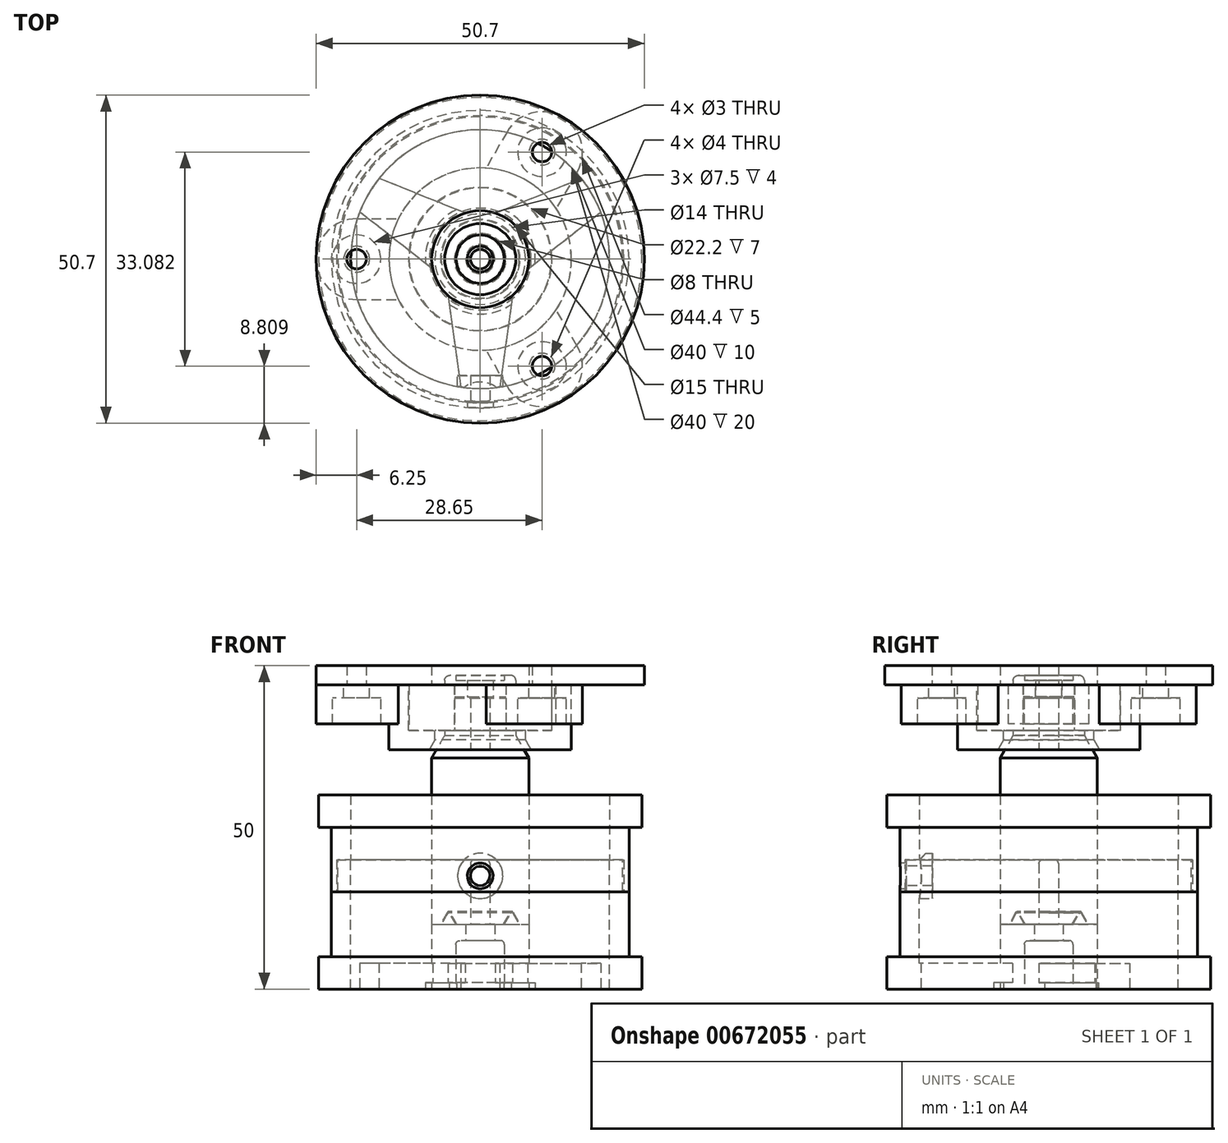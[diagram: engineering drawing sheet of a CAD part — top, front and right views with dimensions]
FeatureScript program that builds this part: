
annotation { "Feature Type Name" : "Feature", "Feature Type Description" : "" }
export const myFeature = defineFeature(function(context is Context, id is Id, definition is map)
    precondition{}
    {
        {
            var Q0;
            Q0=qCreatedBy(makeId("Top.planeOp"),FACE);
            var sketch = newSketch(context, id + "F0", { "sketchPlane" : qUnion([Q0])});
            skCircle(sketch, "E0", {"center": v(0, 0) * mm, "radius": 11.07 * mm});
            skCircle(sketch, "E1", {"center": v(0, 0) * mm, "radius": 13.75 * mm});
            skCircle(sketch, "E2", {"center": v(0, 0) * mm, "radius": 20 * mm});
            skCircle(sketch, "E3", {"center": v(0, 0) * mm, "radius": 25 * mm});
            skCircle(sketch, "E4", {"center": v(0, 0) * mm, "radius": 7.5 * mm});
            skSolve(sketch);
        }
        {
            var Q0;
            Q0=qCreatedBy(makeId("Front.planeOp"),FACE);
            var sketch = newSketch(context, id + "F1", { "sketchPlane" : qUnion([Q0])});
            skPoint(sketch, "E5.0", {"position": v(0, 0) * mm});
            skLineSegment(sketch, "E6", {"start": v(20, 30) * mm, "end": v(20, 0) * mm, "construction": true});
            skLineSegment(sketch, "E7", {"start": v(25, 30) * mm, "end": v(25, 0) * mm, "construction": true});
            skLineSegment(sketch, "E8", {"start": v(25, 30) * mm, "end": v(25, 25) * mm});
            skLineSegment(sketch, "E9", {"start": v(25, 25) * mm, "end": v(23, 25) * mm});
            skLineSegment(sketch, "E10", {"start": v(23, 25) * mm, "end": v(23, 15) * mm});
            skLineSegment(sketch, "E11", {"start": v(25, 30) * mm, "end": v(20, 30) * mm});
            skLineSegment(sketch, "E12", {"start": v(20, 15) * mm, "end": v(20, 30) * mm});
            skLineSegment(sketch, "E13", {"start": v(20, 15) * mm, "end": v(23, 15) * mm});
            skLineSegment(sketch, "E14.MirrorCS", {"start": v(23, 5) * mm, "end": v(23, 15) * mm});
            skLineSegment(sketch, "E15.MirrorCS", {"start": v(25, 0) * mm, "end": v(25, 5) * mm});
            skLineSegment(sketch, "E16.MirrorCS", {"start": v(25, 5) * mm, "end": v(23, 5) * mm});
            skLineSegment(sketch, "E17.MirrorCS", {"start": v(25, 0) * mm, "end": v(20, 0) * mm});
            skLineSegment(sketch, "E18.MirrorCS", {"start": v(20, 15) * mm, "end": v(20, 0) * mm});
            skLineSegment(sketch, "E19", {"start": v(25, 25) * mm, "end": v(25, 5) * mm});
            skSolve(sketch);
        }
        {
            var Q0;
            Q0=qCreatedBy(makeId("Front.planeOp"),FACE);
            var sketch = newSketch(context, id + "F2", { "sketchPlane" : qUnion([Q0])});
            skLineSegment(sketch, "E20.0.0", {"start": v(23, 15) * mm, "end": v(20, 15) * mm});
            skLineSegment(sketch, "E20.0.1", {"start": v(20, 15) * mm, "end": v(20, 0) * mm});
            skLineSegment(sketch, "E20.0.2", {"start": v(20, 0) * mm, "end": v(25, 0) * mm});
            skLineSegment(sketch, "E20.0.3", {"start": v(25, 0) * mm, "end": v(25, 5) * mm});
            skLineSegment(sketch, "E20.0.4", {"start": v(25, 5) * mm, "end": v(23, 5) * mm});
            skLineSegment(sketch, "E20.0.5", {"start": v(23, 5) * mm, "end": v(23, 15) * mm});
            skLineSegment(sketch, "E21", {"start": v(20, 15) * mm, "end": v(20, 20) * mm});
            skLineSegment(sketch, "E22", {"start": v(20, 20) * mm, "end": v(22, 20) * mm});
            skLineSegment(sketch, "E23", {"start": v(22, 20) * mm, "end": v(22, 15) * mm});
            skSolve(sketch);
        }
        {
            var Q0;
            Q0=qCreatedBy(makeId("Front.planeOp"),FACE);
            var sketch = newSketch(context, id + "F3", { "sketchPlane" : qUnion([Q0])});
            skLineSegment(sketch, "E24.0.0", {"start": v(20, 30) * mm, "end": v(20, 15) * mm});
            skLineSegment(sketch, "E24.0.1", {"start": v(20, 15) * mm, "end": v(23, 15) * mm});
            skLineSegment(sketch, "E24.0.2", {"start": v(23, 15) * mm, "end": v(23, 25) * mm});
            skLineSegment(sketch, "E24.0.3", {"start": v(23, 25) * mm, "end": v(25, 25) * mm});
            skLineSegment(sketch, "E24.0.4", {"start": v(25, 25) * mm, "end": v(25, 30) * mm});
            skLineSegment(sketch, "E24.0.5", {"start": v(25, 30) * mm, "end": v(20, 30) * mm});
            skLineSegment(sketch, "E25.0", {"start": v(22.2, 20) * mm, "end": v(22.2, 15) * mm});
            skLineSegment(sketch, "E26.0", {"start": v(20, 20) * mm, "end": v(22, 20) * mm, "construction": true});
            skLineSegment(sketch, "E27", {"start": v(20, 20) * mm, "end": v(22.2, 20) * mm});
            skSolve(sketch);
        }
        {
            var Q0;
            Q0=qCreatedBy(makeId("Top.planeOp"),FACE);
            var sketch = newSketch(context, id + "F4", { "sketchPlane" : qUnion([Q0])});
            skCircle(sketch, "E28", {"center": v(0, 0) * mm, "radius": 2.25 * mm});
            skCircle(sketch, "E29", {"center": v(0, 0) * mm, "radius": 3.75 * mm});
            skCircle(sketch, "E30", {"center": v(0, 0) * mm, "radius": 7.5 * mm});
            skSolve(sketch);
        }
        {
            var Q0;
            Q0=makeQuery(id+"F4.imprint","IMPRINT",FACE,{"disambiguationData":[TD([[makeQuery(id+"F4.imprint","IMPRINT",EDGE,{"derivedFrom":sQuery(id+"F4.wireOp",EDGE,"E29")}),-1.0]])]});
            var Q1;
            Q1=makeQuery(id+"F4.imprint","IMPRINT",FACE,{"disambiguationData":[TD([[makeQuery(id+"F4.imprint","IMPRINT",EDGE,{"derivedFrom":sQuery(id+"F4.wireOp",EDGE,"E28")}),-1.0]])]});
            extrude(context, id + "F5", {"entities" : qUnion([Q0, Q1]), "depth" : 10 * mm, "offsetDistance" : 25 * mm});
        }
        {
            var Q0;
            Q0=makeQuery(id+"F4.imprint","IMPRINT",FACE,{"disambiguationData":[TD([[makeQuery(id+"F4.imprint","IMPRINT",EDGE,{"derivedFrom":sQuery(id+"F4.wireOp",EDGE,"E28")}),-1.0]])]});
            extrude(context, id + "F6", {"entities" : qUnion([Q0]), "operationType" : NewBodyOperationType.REMOVE, "depth" : 7.5 * mm, "offsetDistance" : 25 * mm});
        }
        {
            var Q0;
            Q0=qCreatedBy(makeId("Front.planeOp"),FACE);
            var sketch = newSketch(context, id + "F7", { "sketchPlane" : qUnion([Q0])});
            skLineSegment(sketch, "E31.0.0", {"start": v(-7.5, 10) * mm, "end": v(7.5, 10) * mm});
            skLineSegment(sketch, "E32.0", {"start": v(-20, 0) * mm, "end": v(20, 0) * mm});
            skLineSegment(sketch, "E33", {"start": v(-7.5, 0) * mm, "end": v(-7.5, 10) * mm});
            skLineSegment(sketch, "E34", {"start": v(7.5, 10) * mm, "end": v(7.5, 0) * mm});
            skLineSegment(sketch, "E35", {"start": v(-2.25, 7.5) * mm, "end": v(-2.25, 10) * mm});
            skLineSegment(sketch, "E36", {"start": v(2.25, 10) * mm, "end": v(2.25, 7.5) * mm});
            skLineSegment(sketch, "E37", {"start": v(-2.25, 10) * mm, "end": v(-7.5, 10) * mm});
            skLineSegment(sketch, "E38", {"start": v(-4.88, 10) * mm, "end": v(-4.88, 12) * mm, "construction": true});
            skLineSegment(sketch, "E39", {"start": v(-4.88, 12) * mm, "end": v(-6.03, 10) * mm});
            skLineSegment(sketch, "E40.MirrorCS", {"start": v(-4.88, 12) * mm, "end": v(-3.72, 10) * mm});
            skSolve(sketch);
        }
        {
            var Q0;
            {var subQ0=sQuery(id+"F7.wireOp",EDGE,"E39");Q0=makeQuery(id+"F7.imprint","IMPRINT",FACE,{"disambiguationData":[TD([[makeQuery(id+"F7.imprint","IMPRINT",EDGE,{"derivedFrom":subQ0}),1.0]])]});}
            var Q1;
            Q1=makeQuery(id+"F5.opExtrude","SWEPT_FACE",FACE,{"disambiguationData":[OSD([sQuery(id+"F4.wireOp",EDGE,"E28")])]});
            revolve(context, id + "F8", {"operationType" : NewBodyOperationType.ADD, "entities" : qUnion([Q0]), "axis" : qUnion([Q1]), "revolveType" : RevolveType.FULL});
        }
        {
            var Q0;
            Q0=qCreatedBy(makeId("Front.planeOp"),FACE);
            var sketch = newSketch(context, id + "F9", { "sketchPlane" : qUnion([Q0])});
            skLineSegment(sketch, "E41.0", {"start": v(-7.5, 10) * mm, "end": v(7.5, 10) * mm});
            skLineSegment(sketch, "E42", {"start": v(0, 0) * mm, "end": v(0, 10) * mm, "construction": true});
            skLineSegment(sketch, "E43", {"start": v(0, 10) * mm, "end": v(0, 45) * mm});
            skLineSegment(sketch, "E44", {"start": v(7.5, 10) * mm, "end": v(7.5, 45) * mm});
            skLineSegment(sketch, "E45", {"start": v(7.5, 45) * mm, "end": v(0, 45) * mm});
            skLineSegment(sketch, "E46", {"start": v(7.5, 45) * mm, "end": v(7.5, 40) * mm, "construction": true});
            skLineSegment(sketch, "E47", {"start": v(7.5, 40) * mm, "end": v(0, 40) * mm, "construction": true});
            skLineSegment(sketch, "E48", {"start": v(0, 40) * mm, "end": v(3.95, 40) * mm, "construction": true});
            skLineSegment(sketch, "E49", {"start": v(3.95, 40) * mm, "end": v(3.95, 45) * mm});
            skLineSegment(sketch, "E50", {"start": v(3.95, 40) * mm, "end": v(7.5, 40) * mm});
            skLineSegment(sketch, "E51", {"start": v(0, 10) * mm, "end": v(0, 20) * mm, "construction": true});
            skLineSegment(sketch, "E52", {"start": v(0, 20) * mm, "end": v(1.5, 20) * mm});
            skLineSegment(sketch, "E53", {"start": v(1.5, 20) * mm, "end": v(1.5, 10) * mm});
            skLineSegment(sketch, "E54", {"start": v(1.5, 10) * mm, "end": v(0, 10) * mm});
            skLineSegment(sketch, "E55", {"start": v(0, 45) * mm, "end": v(1.5, 45) * mm});
            skLineSegment(sketch, "E56", {"start": v(1.5, 45) * mm, "end": v(1.5, 40) * mm});
            skLineSegment(sketch, "E57", {"start": v(1.5, 40) * mm, "end": v(0, 40) * mm});
            skLineSegment(sketch, "E58", {"start": v(4.88, 12) * mm, "end": v(3.72, 10) * mm});
            skLineSegment(sketch, "E59", {"start": v(-6.03, 10) * mm, "end": v(-4.88, 12) * mm});
            skLineSegment(sketch, "E60", {"start": v(4.88, 12) * mm, "end": v(6.03, 10) * mm});
            skLineSegment(sketch, "E61.0.0", {"start": v(-3.72, 10) * mm, "end": v(3.72, 10) * mm});
            skLineSegment(sketch, "E62.0", {"start": v(4.88, 12.2) * mm, "end": v(3.6, 10) * mm});
            skLineSegment(sketch, "E62.1", {"start": v(4.88, 12.2) * mm, "end": v(6.15, 10) * mm});
            skLineSegment(sketch, "E63", {"start": v(7.5, 45) * mm, "end": v(7.5, 45.2) * mm, "construction": true});
            skLineSegment(sketch, "E64", {"start": v(7.5, 45.2) * mm, "end": v(0, 45.2) * mm, "construction": true});
            skLineSegment(sketch, "E65", {"start": v(0, 40) * mm, "end": v(5.5, 40) * mm});
            skLineSegment(sketch, "E66", {"start": v(5.5, 40) * mm, "end": v(5.5, 39.2) * mm});
            skLineSegment(sketch, "E67", {"start": v(5.5, 39.2) * mm, "end": v(7.5, 39.2) * mm});
            skLineSegment(sketch, "E68", {"start": v(3.95, 45) * mm, "end": v(3.95, 45.2) * mm, "construction": true});
            skLineSegment(sketch, "E69", {"start": v(3.95, 45.2) * mm, "end": v(3.95, 47) * mm});
            skLineSegment(sketch, "E70", {"start": v(5.5, 40) * mm, "end": v(5.5, 47) * mm, "construction": true});
            skLineSegment(sketch, "E71", {"start": v(5.5, 47) * mm, "end": v(3.95, 47) * mm});
            skLineSegment(sketch, "E72", {"start": v(5.5, 47) * mm, "end": v(5.5, 48.5) * mm});
            skLineSegment(sketch, "E73", {"start": v(5.5, 48.5) * mm, "end": v(0, 48.5) * mm});
            skLineSegment(sketch, "E74", {"start": v(0, 48.5) * mm, "end": v(0, 45.2) * mm});
            skLineSegment(sketch, "E75", {"start": v(3.95, 45.2) * mm, "end": v(0, 45.2) * mm});
            skLineSegment(sketch, "E76", {"start": v(0, 48.5) * mm, "end": v(1.88, 48.5) * mm});
            skLineSegment(sketch, "E77", {"start": v(0, 45.2) * mm, "end": v(2, 45.2) * mm, "construction": true});
            skLineSegment(sketch, "E78", {"start": v(2, 45.2) * mm, "end": v(2, 47.7) * mm});
            skLineSegment(sketch, "E79", {"start": v(0, 48.5) * mm, "end": v(3.75, 48.5) * mm, "construction": true});
            skLineSegment(sketch, "E80", {"start": v(3.75, 48.5) * mm, "end": v(3.75, 47.7) * mm});
            skLineSegment(sketch, "E81", {"start": v(3.75, 47.7) * mm, "end": v(2, 47.7) * mm});
            skLineSegment(sketch, "E82", {"start": v(5.5, 39.2) * mm, "end": v(7.5, 35.74) * mm});
            skLineSegment(sketch, "E83", {"start": v(1.5, 40) * mm, "end": v(1.5, 37) * mm});
            skLineSegment(sketch, "E84", {"start": v(1.5, 37) * mm, "end": v(0, 37) * mm});
            skSolve(sketch);
        }
        {
            var Q0;
            {var subQ4=sQuery(id+"F9.wireOp",EDGE,"E52");Q0=makeQuery(id+"F9.imprint","IMPRINT",FACE,{"disambiguationData":[TD([[makeQuery(id+"F9.imprint","IMPRINT",EDGE,{"derivedFrom":subQ4}),1.0]])]});}
            var Q1;
            {var subQ2=sQuery(id+"F9.wireOp",EDGE,"E49");Q1=makeQuery(id+"F9.imprint","IMPRINT",FACE,{"disambiguationData":[TD([[makeQuery(id+"F9.imprint","IMPRINT",EDGE,{"derivedFrom":subQ2}),1.0]])]});}
            var Q2;
            {var subQ3=sQuery(id+"F9.wireOp",EDGE,"E69");Q2=makeQuery(id+"F9.imprint","IMPRINT",FACE,{"disambiguationData":[TD([[makeQuery(id+"F9.imprint","IMPRINT",EDGE,{"derivedFrom":subQ3}),1.0]])]});}
            var Q3;
            Q3=sQuery(id+"F9.wireOp",EDGE,"E43");
            revolve(context, id + "F10", {"entities" : qUnion([Q0, Q1, Q2]), "axis" : qUnion([Q3]), "revolveType" : RevolveType.FULL});
        }
        {
            var Q0;
            Q0=makeQuery(id+"F8.opRevolve","SWEPT_EDGE",EDGE,{"disambiguationData":[OSD([sQuery(id+"F7.wireOp",EDGE,"E39"),sQuery(id+"F7.wireOp",EDGE,"E40.MirrorCS")])]});
            var Q1;
            Q1=makeQuery(id+"F10.opRevolve","SWEPT_EDGE",EDGE,{"disambiguationData":[OSD([sQuery(id+"F9.wireOp",EDGE,"E62.0"),sQuery(id+"F9.wireOp",EDGE,"E62.1")])]});
            fillet(context, id + "F11", {"entities" : qUnion([Q0, Q1]), "radius" : .2 * mm, "tangentPropagation" : true, "allowEdgeOverflow" : false});
        }
        {
            var Q0;
            Q0=makeQuery(id+"F10.opRevolve","SWEPT_EDGE",EDGE,{"disambiguationData":[OSD([sQuery(id+"F9.wireOp",EDGE,"E52"),sQuery(id+"F9.wireOp",EDGE,"E53")])]});
            var Q1;
            Q1=makeQuery(id+"F6.boolean.opBoolean","COPY",EDGE,{"derivedFrom":makeQuery(id+"F6.opExtrude","CAP_EDGE",EDGE,{"disambiguationData":[OSD([sQuery(id+"F4.wireOp",EDGE,"E28")])],"isStart":false})});
            var Q2;
            Q2=makeQuery(id+"F6.boolean.opBoolean","COPY",EDGE,{"derivedFrom":makeQuery(id+"F6.opExtrude","CAP_EDGE",EDGE,{"disambiguationData":[OSD([sQuery(id+"F4.wireOp",EDGE,"E29")])],"isStart":false})});
            fillet(context, id + "F12", {"entities" : qUnion([Q0, Q1, Q2]), "radius" : .6 * mm, "tangentPropagation" : true, "allowEdgeOverflow" : false});
        }
        {
            var Q0;
            Q0=makeQuery(id+"F10.opRevolve","SWEPT_EDGE",EDGE,{"disambiguationData":[OSD([sQuery(id+"F9.wireOp",EDGE,"E72"),sQuery(id+"F9.wireOp",EDGE,"E73")])]});
            fillet(context, id + "F13", {"entities" : qUnion([Q0]), "radius" : .8 * mm, "tangentPropagation" : true, "allowEdgeOverflow" : false});
        }
        {
            var Q0;
            Q0=qCreatedBy(makeId("Front.planeOp"),FACE);
            var sketch = newSketch(context, id + "F14", { "sketchPlane" : qUnion([Q0])});
            skLineSegment(sketch, "E85.0.0", {"start": v(-5.5, 40) * mm, "end": v(5.5, 40) * mm, "construction": true});
            skLineSegment(sketch, "E86", {"start": v(-3.95, 40) * mm, "end": v(-3.95, 45) * mm, "construction": true});
            skLineSegment(sketch, "E87", {"start": v(3.95, 45) * mm, "end": v(3.95, 40) * mm, "construction": true});
            skLineSegment(sketch, "E88.0.0", {"start": v(5.5, 47) * mm, "end": v(-5.5, 47) * mm, "construction": true});
            skLineSegment(sketch, "E89", {"start": v(-3.95, 45.2) * mm, "end": v(-3.95, 47) * mm, "construction": true});
            skLineSegment(sketch, "E90", {"start": v(3.95, 47) * mm, "end": v(3.95, 45.2) * mm, "construction": true});
            skLineSegment(sketch, "E91", {"start": v(-5.5, 47) * mm, "end": v(-5.5, 40) * mm});
            skLineSegment(sketch, "E92", {"start": v(0, 40) * mm, "end": v(0, 47) * mm, "construction": true});
            skLineSegment(sketch, "E93", {"start": v(0, 43.5) * mm, "end": v(-11, 43.5) * mm, "construction": true});
            skLineSegment(sketch, "E94", {"start": v(-11, 43.5) * mm, "end": v(-11, 47) * mm});
            skLineSegment(sketch, "E95", {"start": v(-11, 47) * mm, "end": v(-5.5, 47) * mm});
            skLineSegment(sketch, "E96", {"start": v(-11, 43.5) * mm, "end": v(-11, 40) * mm});
            skLineSegment(sketch, "E97", {"start": v(-11, 40) * mm, "end": v(-5.5, 40) * mm});
            skLineSegment(sketch, "E98", {"start": v(-3.95, 40) * mm, "end": v(-3.95, 47) * mm});
            skLineSegment(sketch, "E99", {"start": v(0, 43.5) * mm, "end": v(-4, 43.5) * mm, "construction": true});
            skLineSegment(sketch, "E100", {"start": v(-4, 43.5) * mm, "end": v(-4, 47) * mm});
            skLineSegment(sketch, "E101", {"start": v(-4, 47) * mm, "end": v(-5.5, 47) * mm});
            skLineSegment(sketch, "E102", {"start": v(-4, 43.5) * mm, "end": v(-4, 40) * mm});
            skLineSegment(sketch, "E103", {"start": v(-4, 40) * mm, "end": v(-5.5, 40) * mm});
            skSolve(sketch);
        }
        {
            var Q0;
            Q0=makeQuery(id+"F14.imprint","IMPRINT",FACE,{"disambiguationData":[TD([[makeQuery(id+"F14.imprint","IMPRINT",EDGE,{"derivedFrom":sQuery(id+"F14.wireOp",EDGE,"E91")}),-1.0]])]});
            var Q1;
            Q1=makeQuery(id+"F14.imprint","IMPRINT",FACE,{"disambiguationData":[TD([[makeQuery(id+"F14.imprint","IMPRINT",EDGE,{"derivedFrom":sQuery(id+"F14.wireOp",EDGE,"E91")}),1.0]])]});
            var Q2;
            Q2=sQuery(id+"F14.wireOp",EDGE,"E92");
            revolve(context, id + "F15", {"entities" : qUnion([Q0, Q1]), "axis" : qUnion([Q2]), "revolveType" : RevolveType.FULL});
        }
        {
            var Q0;
            Q0=qCreatedBy(makeId("Front.planeOp"),FACE);
            var sketch = newSketch(context, id + "F16", { "sketchPlane" : qUnion([Q0])});
            skLineSegment(sketch, "E104", {"start": v(-1.5, 40) * mm, "end": v(-1.5, 45) * mm, "construction": true});
            skLineSegment(sketch, "E105", {"start": v(1.5, 45) * mm, "end": v(1.5, 40) * mm, "construction": true});
            skLineSegment(sketch, "E106.0.0", {"start": v(3.95, 40) * mm, "end": v(-3.95, 40) * mm, "construction": true});
            skLineSegment(sketch, "E107.0.0", {"start": v(-3.95, 45) * mm, "end": v(3.95, 45) * mm, "construction": true});
            skLineSegment(sketch, "E108", {"start": v(0, 45) * mm, "end": v(0, 40) * mm, "construction": true});
            skLineSegment(sketch, "E109.0.0", {"start": v(11, 40) * mm, "end": v(-11, 40) * mm, "construction": true});
            skLineSegment(sketch, "E110", {"start": v(-11, 40) * mm, "end": v(-11, 47) * mm, "construction": true});
            skLineSegment(sketch, "E111", {"start": v(11, 47) * mm, "end": v(11, 40) * mm, "construction": true});
            skLineSegment(sketch, "E112", {"start": v(-7.5, 35.74) * mm, "end": v(-5.5, 39.2) * mm, "construction": true});
            skLineSegment(sketch, "E113", {"start": v(5.5, 39.2) * mm, "end": v(7.5, 35.74) * mm, "construction": true});
            skLineSegment(sketch, "E114", {"start": v(-5.5, 39.2) * mm, "end": v(-5.5, 40) * mm, "construction": true});
            skLineSegment(sketch, "E115", {"start": v(5.5, 40) * mm, "end": v(5.5, 39.2) * mm, "construction": true});
            skLineSegment(sketch, "E116", {"start": v(-5.5, 40) * mm, "end": v(-7, 40) * mm, "construction": true});
            skLineSegment(sketch, "E117", {"start": v(-7, 40) * mm, "end": v(-7, 38.5) * mm});
            skLineSegment(sketch, "E118", {"start": v(0, 40) * mm, "end": v(-11.1, 40) * mm});
            skLineSegment(sketch, "E119", {"start": v(-11.1, 40) * mm, "end": v(-11.1, 47.44) * mm});
            skLineSegment(sketch, "E120", {"start": v(-11.1, 47) * mm, "end": v(-14.1, 47) * mm});
            skLineSegment(sketch, "E121", {"start": v(-7, 38.5) * mm, "end": v(-7.87, 37) * mm});
            skLineSegment(sketch, "E122", {"start": v(-7.87, 37) * mm, "end": v(-14.1, 37) * mm});
            skLineSegment(sketch, "E123", {"start": v(-14.1, 37) * mm, "end": v(-14.1, 47) * mm});
            skLineSegment(sketch, "E124", {"start": v(-14.1, 47) * mm, "end": v(-24.1, 47) * mm});
            skLineSegment(sketch, "E125", {"start": v(-24.1, 47) * mm, "end": v(-24.1, 44) * mm});
            skLineSegment(sketch, "E126", {"start": v(-24.1, 44) * mm, "end": v(-14.1, 44) * mm});
            skSolve(sketch);
        }
        {
            var Q0;
            {var subQ4=sQuery(id+"F16.wireOp",EDGE,"E117");Q0=makeQuery(id+"F16.imprint","IMPRINT",FACE,{"disambiguationData":[TD([[makeQuery(id+"F16.imprint","IMPRINT",EDGE,{"derivedFrom":subQ4}),-1.0]])]});}
            var Q1;
            Q1=sQuery(id+"F16.wireOp",EDGE,"E108");
            revolve(context, id + "F17", {"entities" : qUnion([Q0]), "axis" : qUnion([Q1]), "revolveType" : RevolveType.FULL});
        }
        {
            var Q0;
            Q0=makeQuery(id+"F17.opRevolve","SWEPT_FACE",FACE,{"disambiguationData":[OSD([sQuery(id+"F16.wireOp",EDGE,"E120")])]});
            var sketch = newSketch(context, id + "F18", { "sketchPlane" : qUnion([Q0])});
            skCircle(sketch, "E127.0", {"center": v(0, 0) * mm, "radius": 14.1 * mm, "construction": true});
            skLineSegment(sketch, "E128.0", {"start": v(-24.1, 0) * mm, "end": v(-14.1, 0) * mm, "construction": true});
            skCircle(sketch, "E129", {"center": v(-19.1, 0) * mm, "radius": 3.75 * mm});
            skCircle(sketch, "E130", {"center": v(-19.1, 0) * mm, "radius": 2 * mm});
            skCircle(sketch, "E131", {"center": v(-19.1, 0) * mm, "radius": 6.25 * mm});
            skLineSegment(sketch, "E132", {"start": v(-19.1, 0) * mm, "end": v(-19.1, 6.25) * mm, "construction": true});
            skLineSegment(sketch, "E133", {"start": v(-19.1, 0) * mm, "end": v(-19.1, -6.25) * mm, "construction": true});
            skLineSegment(sketch, "E134", {"start": v(-19.1, -6.25) * mm, "end": v(-12.64, -6.25) * mm});
            skLineSegment(sketch, "E135", {"start": v(-19.1, 6.25) * mm, "end": v(-12.64, 6.25) * mm});
            skLineSegment(sketch, "E136", {"start": v(0, 0) * mm, "end": v(0, 7.47) * mm});
            skCircle(sketch, "E137.MirrorC", {"center": v(19.1, 0) * mm, "radius": 6.25 * mm});
            skCircle(sketch, "E138.MirrorC", {"center": v(19.1, 0) * mm, "radius": 2 * mm});
            skCircle(sketch, "E139.MirrorC", {"center": v(19.1, 0) * mm, "radius": 3.75 * mm});
            skLineSegment(sketch, "E140.MirrorCS", {"start": v(19.1, 6.25) * mm, "end": v(12.64, 6.25) * mm});
            skLineSegment(sketch, "E141.MirrorCS", {"start": v(19.1, -6.25) * mm, "end": v(12.64, -6.25) * mm});
            skSolve(sketch);
        }
        {
            var Q0;
            Q0=makeQuery(id+"F18.imprint","IMPRINT",FACE,{"disambiguationData":[TD([[makeQuery(id+"F18.imprint","IMPRINT",EDGE,{"derivedFrom":sQuery(id+"F18.wireOp",EDGE,"E129")}),1.0]])]});
            var Q1;
            Q1=makeQuery(id+"F18.imprint","IMPRINT",FACE,{"disambiguationData":[TD([[makeQuery(id+"F18.imprint","IMPRINT",EDGE,{"derivedFrom":sQuery(id+"F18.wireOp",EDGE,"E129")}),-1.0]])]});
            var Q2;
            {var subQ0=sQuery(id+"F18.wireOp",EDGE,"E134");Q2=makeQuery(id+"F18.imprint","IMPRINT",FACE,{"disambiguationData":[TD([[makeQuery(id+"F18.imprint","IMPRINT",EDGE,{"derivedFrom":subQ0}),1.0]])]});}
            var Q3;
            {var subQ0=sQuery(id+"F18.wireOp",EDGE,"E135");Q3=makeQuery(id+"F18.imprint","IMPRINT",FACE,{"disambiguationData":[TD([[makeQuery(id+"F18.imprint","IMPRINT",EDGE,{"derivedFrom":subQ0}),-1.0]])]});}
            extrude(context, id + "F19", {"entities" : qUnion([Q0, Q1, Q2, Q3]), "oppositeDirection" : true, "depth" : 2 * mm, "offsetDistance" : 25 * mm});
        }
        {
            var Q0;
            Q0=makeQuery(id+"F18.imprint","IMPRINT",FACE,{"disambiguationData":[TD([[makeQuery(id+"F18.imprint","IMPRINT",EDGE,{"derivedFrom":sQuery(id+"F18.wireOp",EDGE,"E129")}),-1.0]])]});
            var Q1;
            {var subQ0=sQuery(id+"F18.wireOp",EDGE,"E135");Q1=makeQuery(id+"F18.imprint","IMPRINT",FACE,{"disambiguationData":[TD([[makeQuery(id+"F18.imprint","IMPRINT",EDGE,{"derivedFrom":subQ0}),-1.0]])]});}
            var Q2;
            {var subQ0=sQuery(id+"F18.wireOp",EDGE,"E134");Q2=makeQuery(id+"F18.imprint","IMPRINT",FACE,{"disambiguationData":[TD([[makeQuery(id+"F18.imprint","IMPRINT",EDGE,{"derivedFrom":subQ0}),1.0]])]});}
            extrude(context, id + "F20", {"entities" : qUnion([Q0, Q1, Q2]), "oppositeDirection" : true, "depth" : 6 * mm, "offsetDistance" : 25 * mm});
        }
        {
            var Q0;
            Q0=makeQuery(id+"F20.opExtrude","SWEPT_BODY",BODY,{"disambiguationData":[OSD([sQuery(id+"F16.wireOp",EDGE,"E120"),sQuery(id+"F16.wireOp",EDGE,"E123"),sQuery(id+"F16.wireOp",EDGE,"E124"),sQuery(id+"F18.wireOp",EDGE,"E129"),sQuery(id+"F18.wireOp",EDGE,"E131"),sQuery(id+"F18.wireOp",EDGE,"E134"),sQuery(id+"F18.wireOp",EDGE,"E135")])]});
            var Q1;
            Q1=makeQuery(id+"F19.opExtrude","SWEPT_BODY",BODY,{"disambiguationData":[OSD([sQuery(id+"F16.wireOp",EDGE,"E120"),sQuery(id+"F16.wireOp",EDGE,"E123"),sQuery(id+"F16.wireOp",EDGE,"E124"),sQuery(id+"F18.wireOp",EDGE,"E130"),sQuery(id+"F18.wireOp",EDGE,"E131"),sQuery(id+"F18.wireOp",EDGE,"E134"),sQuery(id+"F18.wireOp",EDGE,"E135")])]});
            booleanBodies(context, id + "F21", {"operationType" : BooleanOperationType.UNION, "tools" : qUnion([Q0, Q1])});
        }
        {
            var Q0;
            Q0=makeQuery(id+"F20.opExtrude","SWEPT_BODY",BODY,{"disambiguationData":[OSD([sQuery(id+"F16.wireOp",EDGE,"E120"),sQuery(id+"F16.wireOp",EDGE,"E123"),sQuery(id+"F16.wireOp",EDGE,"E124"),sQuery(id+"F18.wireOp",EDGE,"E129"),sQuery(id+"F18.wireOp",EDGE,"E131"),sQuery(id+"F18.wireOp",EDGE,"E134"),sQuery(id+"F18.wireOp",EDGE,"E135")])]});
            var Q1;
            Q1=sQuery(id+"F16.wireOp",EDGE,"E108");
            circularPattern(context, id + "F22", {"entities" : qUnion([Q0]), "axis" : qUnion([Q1]), "angle" : 360 * degree, "instanceCount" : 3, "equalSpace" : true});
        }
        {
            var Q0;
            Q0=makeQuery(id+"F17.opRevolve","SWEPT_BODY",BODY,{"disambiguationData":[OSD([sQuery(id+"F16.wireOp",EDGE,"E117"),sQuery(id+"F16.wireOp",EDGE,"E118"),sQuery(id+"F16.wireOp",EDGE,"E119"),sQuery(id+"F16.wireOp",EDGE,"E120"),sQuery(id+"F16.wireOp",EDGE,"E121"),sQuery(id+"F16.wireOp",EDGE,"E122"),sQuery(id+"F16.wireOp",EDGE,"E123")])]});
            var Q1;
            Q1=makeQuery(id+"F20.opExtrude","SWEPT_BODY",BODY,{"disambiguationData":[OSD([sQuery(id+"F16.wireOp",EDGE,"E120"),sQuery(id+"F16.wireOp",EDGE,"E123"),sQuery(id+"F16.wireOp",EDGE,"E124"),sQuery(id+"F18.wireOp",EDGE,"E129"),sQuery(id+"F18.wireOp",EDGE,"E131"),sQuery(id+"F18.wireOp",EDGE,"E134"),sQuery(id+"F18.wireOp",EDGE,"E135")])]});
            var Q2;
            Q2=makeQuery(id+"F22.opPattern","COPY",BODY,{"derivedFrom":makeQuery(id+"F20.opExtrude","SWEPT_BODY",BODY,{"disambiguationData":[OSD([sQuery(id+"F16.wireOp",EDGE,"E120"),sQuery(id+"F16.wireOp",EDGE,"E123"),sQuery(id+"F16.wireOp",EDGE,"E124"),sQuery(id+"F18.wireOp",EDGE,"E129"),sQuery(id+"F18.wireOp",EDGE,"E131"),sQuery(id+"F18.wireOp",EDGE,"E134"),sQuery(id+"F18.wireOp",EDGE,"E135")])]}),"instanceName":"2"});
            var Q3;
            Q3=makeQuery(id+"F22.opPattern","COPY",BODY,{"derivedFrom":makeQuery(id+"F20.opExtrude","SWEPT_BODY",BODY,{"disambiguationData":[OSD([sQuery(id+"F16.wireOp",EDGE,"E120"),sQuery(id+"F16.wireOp",EDGE,"E123"),sQuery(id+"F16.wireOp",EDGE,"E124"),sQuery(id+"F18.wireOp",EDGE,"E129"),sQuery(id+"F18.wireOp",EDGE,"E131"),sQuery(id+"F18.wireOp",EDGE,"E134"),sQuery(id+"F18.wireOp",EDGE,"E135")])]}),"instanceName":"1"});
            booleanBodies(context, id + "F23", {"operationType" : BooleanOperationType.UNION, "tools" : qUnion([Q0, Q1, Q2, Q3])});
        }
        {
            var Q0;
            Q0=makeQuery(id+"F1.imprint","IMPRINT",FACE,{"disambiguationData":[TD([[makeQuery(id+"F1.imprint","IMPRINT",EDGE,{"derivedFrom":sQuery(id+"F1.wireOp",EDGE,"E15.MirrorCS")}),1.0]])]});
            var Q1;
            {var subQ0=sQuery(id+"F2.wireOp",EDGE,"E21");Q1=makeQuery(id+"F2.imprint","IMPRINT",FACE,{"disambiguationData":[TD([[makeQuery(id+"F2.imprint","IMPRINT",EDGE,{"derivedFrom":subQ0}),-1.0]])]});}
            var Q2;
            Q2=makeQuery(id+"F5.opExtrude","SWEPT_FACE",FACE,{"disambiguationData":[OSD([sQuery(id+"F4.wireOp",EDGE,"E30")])]});
            revolve(context, id + "F24", {"entities" : qUnion([Q0, Q1]), "axis" : qUnion([Q2]), "revolveType" : RevolveType.FULL});
        }
        {
            var Q0;
            Q0=makeQuery(id+"F24.opRevolve","SWEPT_BODY",BODY,{"disambiguationData":[OSD([sQuery(id+"F1.wireOp",EDGE,"E15.MirrorCS"),sQuery(id+"F1.wireOp",EDGE,"E16.MirrorCS"),sQuery(id+"F1.wireOp",EDGE,"E14.MirrorCS"),sQuery(id+"F1.wireOp",EDGE,"E17.MirrorCS"),sQuery(id+"F1.wireOp",EDGE,"E13"),sQuery(id+"F1.wireOp",EDGE,"E18.MirrorCS")])]});
            var Q1;
            Q1=makeQuery(id+"F24.opRevolve","SWEPT_BODY",BODY,{"disambiguationData":[OSD([sQuery(id+"F2.wireOp",EDGE,"E20.0.0"),sQuery(id+"F2.wireOp",EDGE,"E21"),sQuery(id+"F2.wireOp",EDGE,"E22"),sQuery(id+"F2.wireOp",EDGE,"E23")])]});
            booleanBodies(context, id + "F25", {"operationType" : BooleanOperationType.UNION, "tools" : qUnion([Q0, Q1])});
        }
        {
            var Q0;
            Q0=qCreatedBy(makeId("Front.planeOp"),FACE);
            cPlane(context, id + "F26", {"entities" : qUnion([Q0]), "cplaneType" : CPlaneType.OFFSET, "offset" : 25 * mm, "width" : 150 * mm, "height" : 150 * mm});
        }
        {
            var Q0;
            Q0=qCreatedBy(id+"F26.planeOp",FACE);
            var sketch = newSketch(context, id + "F27", { "sketchPlane" : qUnion([Q0])});
            skLineSegment(sketch, "E142.0", {"start": v(-22, 20) * mm, "end": v(22, 20) * mm, "construction": true});
            skLineSegment(sketch, "E143.0", {"start": v(-23, 15) * mm, "end": v(23, 15) * mm, "construction": true});
            skLineSegment(sketch, "E144", {"start": v(0, 15) * mm, "end": v(0, 20) * mm, "construction": true});
            skCircle(sketch, "E145", {"center": v(0, 17.5) * mm, "radius": 1.5 * mm});
            skCircle(sketch, "E146", {"center": v(0, 17.5) * mm, "radius": 2 * mm});
            skCircle(sketch, "E147", {"center": v(0, 17.5) * mm, "radius": 3.75 * mm});
            skSolve(sketch);
        }
        {
            var Q0;
            Q0=makeQuery(id+"F27.imprint","IMPRINT",FACE,{"disambiguationData":[TD([[makeQuery(id+"F27.imprint","IMPRINT",EDGE,{"derivedFrom":sQuery(id+"F27.wireOp",EDGE,"E145")}),1.0]])]});
            var Q1;
            Q1=makeQuery(id+"F10.opRevolve","SWEPT_FACE",FACE,{"disambiguationData":[OSD([sQuery(id+"F9.wireOp",EDGE,"E44")])]});
            extrude(context, id + "F28", {"entities" : qUnion([Q0]), "operationType" : NewBodyOperationType.REMOVE, "endBound" : BoundingType.UP_TO_SURFACE, "oppositeDirection" : true, "depth" : 25 * mm, "endBoundEntityFace" : qUnion([Q1]), "offsetDistance" : 25 * mm});
        }
        {
            var Q0;
            Q0=qCreatedBy(id+"F26.planeOp",FACE);
            cPlane(context, id + "F29", {"entities" : qUnion([Q0]), "cplaneType" : CPlaneType.OFFSET, "offset" : 7 * mm, "oppositeDirection" : true, "width" : 150 * mm, "height" : 150 * mm});
        }
        {
            var Q0;
            Q0=qCreatedBy(id+"F29.planeOp",FACE);
            var sketch = newSketch(context, id + "F30", { "sketchPlane" : qUnion([Q0])});
            skCircle(sketch, "E148.0", {"center": v(0, 17.5) * mm, "radius": 1.5 * mm});
            skCircle(sketch, "E149", {"center": v(0, 17.5) * mm, "radius": 3.5 * mm});
            skSolve(sketch);
        }
        {
            var Q0;
            Q0=makeQuery(id+"F30.imprint","IMPRINT",FACE,{"disambiguationData":[TD([[makeQuery(id+"F30.imprint","IMPRINT",EDGE,{"derivedFrom":sQuery(id+"F30.wireOp",EDGE,"E148.0")}),-1.0]])]});
            var Q1;
            Q1=makeQuery(id+"F25.opBoolean","MERGE",FACE,{"derivedFrom":[makeQuery(id+"F24.opRevolve","SWEPT_FACE",FACE,{"disambiguationData":[OSD([sQuery(id+"F1.wireOp",EDGE,"E18.MirrorCS")])]}),makeQuery(id+"F24.opRevolve","SWEPT_FACE",FACE,{"disambiguationData":[OSD([sQuery(id+"F2.wireOp",EDGE,"E21")])]})]});
            extrude(context, id + "F31", {"entities" : qUnion([Q0]), "operationType" : NewBodyOperationType.ADD, "endBound" : BoundingType.UP_TO_SURFACE, "depth" : 25 * mm, "endBoundEntityFace" : qUnion([Q1]), "offsetDistance" : 25 * mm});
        }
        {
            var Q0;
            Q0=qCreatedBy(makeId("Right.planeOp"),FACE);
            var sketch = newSketch(context, id + "F32", { "sketchPlane" : qUnion([Q0])});
            skLineSegment(sketch, "E150.0.0", {"start": v(-22, 20) * mm, "end": v(22, 20) * mm});
            skLineSegment(sketch, "E151", {"start": v(-20, 21) * mm, "end": v(-18, 21) * mm});
            skLineSegment(sketch, "E152", {"start": v(-20, 20) * mm, "end": v(-20, 21) * mm});
            skLineSegment(sketch, "E153", {"start": v(-20, 20) * mm, "end": v(-19, 21) * mm});
            skSolve(sketch);
        }
        {
            var Q0;
            {var subQ0=sQuery(id+"F32.wireOp",EDGE,"E152");Q0=makeQuery(id+"F32.imprint","IMPRINT",FACE,{"disambiguationData":[TD([[makeQuery(id+"F32.imprint","IMPRINT",EDGE,{"derivedFrom":subQ0}),-1.0]])]});}
            var Q1;
            Q1=makeQuery(id+"F25.opBoolean","MERGE",FACE,{"derivedFrom":[makeQuery(id+"F24.opRevolve","SWEPT_FACE",FACE,{"disambiguationData":[OSD([sQuery(id+"F1.wireOp",EDGE,"E18.MirrorCS")])]}),makeQuery(id+"F24.opRevolve","SWEPT_FACE",FACE,{"disambiguationData":[OSD([sQuery(id+"F2.wireOp",EDGE,"E21")])]})]});
            revolve(context, id + "F33", {"operationType" : NewBodyOperationType.REMOVE, "entities" : qUnion([Q0]), "axis" : qUnion([Q1]), "revolveType" : RevolveType.FULL, "oppositeDirection" : true});
        }
        {
            var Q0;
            {var subQ0=sQuery(id+"F3.wireOp",EDGE,"E24.0.2");Q0=makeQuery(id+"F3.imprint","IMPRINT",FACE,{"disambiguationData":[TD([[makeQuery(id+"F3.imprint","IMPRINT",EDGE,{"derivedFrom":subQ0}),1.0]])]});}
            var Q1;
            Q1=makeQuery(id+"F6.boolean.opBoolean","COPY",FACE,{"derivedFrom":makeQuery(id+"F6.opExtrude","SWEPT_FACE",FACE,{"disambiguationData":[OSD([sQuery(id+"F4.wireOp",EDGE,"E29")])]})});
            revolve(context, id + "F34", {"entities" : qUnion([Q0]), "axis" : qUnion([Q1]), "revolveType" : RevolveType.FULL});
        }
        {
            var Q0;
            Q0=qCreatedBy(id+"F26.planeOp",FACE);
            var sketch = newSketch(context, id + "F35", { "sketchPlane" : qUnion([Q0])});
            skCircle(sketch, "E154.0", {"center": v(0, 17.5) * mm, "radius": 2 * mm});
            skCircle(sketch, "E155.0", {"center": v(0, 17.5) * mm, "radius": 3.75 * mm});
            skSolve(sketch);
        }
        {
            var Q0;
            Q0=makeQuery(id+"F27.imprint","IMPRINT",FACE,{"disambiguationData":[TD([[makeQuery(id+"F27.imprint","IMPRINT",EDGE,{"derivedFrom":sQuery(id+"F27.wireOp",EDGE,"E145")}),-1.0]])]});
            var Q1;
            Q1=makeQuery(id+"F35.imprint","IMPRINT",FACE,{"disambiguationData":[TD([[makeQuery(id+"F35.imprint","IMPRINT",EDGE,{"derivedFrom":sQuery(id+"F35.wireOp",EDGE,"E154.0")}),1.0]])]});
            var Q2;
            Q2=makeQuery(id+"F24.opRevolve","SWEPT_FACE",FACE,{"disambiguationData":[OSD([sQuery(id+"F2.wireOp",EDGE,"E23")])]});
            var Q3;
            Q3=makeQuery(id+"F24.opRevolve","SWEPT_BODY",BODY,{"disambiguationData":[OSD([sQuery(id+"F1.wireOp",EDGE,"E15.MirrorCS"),sQuery(id+"F1.wireOp",EDGE,"E16.MirrorCS"),sQuery(id+"F1.wireOp",EDGE,"E14.MirrorCS"),sQuery(id+"F1.wireOp",EDGE,"E17.MirrorCS"),sQuery(id+"F1.wireOp",EDGE,"E13"),sQuery(id+"F1.wireOp",EDGE,"E18.MirrorCS")])]});
            extrude(context, id + "F36", {"entities" : qUnion([Q0, Q1]), "operationType" : NewBodyOperationType.REMOVE, "endBound" : BoundingType.UP_TO_SURFACE, "oppositeDirection" : true, "depth" : 25 * mm, "endBoundEntityFace" : qUnion([Q2]), "endBoundEntityBody" : qUnion([Q3]), "offsetDistance" : 25 * mm});
        }
        {
            var Q0;
            Q0=makeQuery(id+"F4.imprint","IMPRINT",FACE,{"disambiguationData":[TD([[makeQuery(id+"F4.imprint","IMPRINT",EDGE,{"derivedFrom":sQuery(id+"F4.wireOp",EDGE,"E29")}),-1.0]])]});
            var sketch = newSketch(context, id + "F37", { "sketchPlane" : qUnion([Q0])});
            skCircle(sketch, "E156.0", {"center": v(0, 0) * mm, "radius": 20 * mm});
            skCircle(sketch, "E157.0", {"center": v(0, 0) * mm, "radius": 7.5 * mm});
            skLineSegment(sketch, "E158", {"start": v(0, 0) * mm, "end": v(0, -20) * mm, "construction": true});
            skLineSegment(sketch, "E159", {"start": v(0, -20) * mm, "end": v(5, -20) * mm, "construction": true});
            skLineSegment(sketch, "E160", {"start": v(5, -19.36) * mm, "end": v(5, -5.6) * mm});
            skLineSegment(sketch, "E161.MirrorCS", {"start": v(-5, -19.36) * mm, "end": v(-5, -5.6) * mm});
            skPoint(sketch, "E162.orphan", {"position": v(-5, -20) * mm});
            skLineSegment(sketch, "E163.1.0", {"start": v(19.27, 5.35) * mm, "end": v(7.34, -1.54) * mm});
            skLineSegment(sketch, "E163.1.1", {"start": v(14.27, 14.01) * mm, "end": v(2.34, 7.13) * mm});
            skLineSegment(sketch, "E163.2.0", {"start": v(-14.27, 14.01) * mm, "end": v(-2.34, 7.13) * mm});
            skLineSegment(sketch, "E163.2.1", {"start": v(-19.27, 5.35) * mm, "end": v(-7.34, -1.54) * mm});
            skLineSegment(sketch, "E164", {"start": v(5, -5.6) * mm, "end": v(3, -19.77) * mm});
            skLineSegment(sketch, "E165.MirrorCS", {"start": v(-5, -5.6) * mm, "end": v(-3, -19.77) * mm});
            skLineSegment(sketch, "E166.1.0", {"start": v(7.34, -1.54) * mm, "end": v(18.63, 7.28) * mm});
            skLineSegment(sketch, "E166.1.1", {"start": v(2.34, 7.13) * mm, "end": v(15.62, 12.5) * mm});
            skLineSegment(sketch, "E166.2.0", {"start": v(-2.34, 7.13) * mm, "end": v(-15.62, 12.5) * mm});
            skLineSegment(sketch, "E166.2.1", {"start": v(-7.34, -1.54) * mm, "end": v(-18.63, 7.28) * mm});
            skSolve(sketch);
        }
        {
            var Q0;
            {var subQ0=sQuery(id+"F37.wireOp",EDGE,"E164");Q0=makeQuery(id+"F37.imprint","IMPRINT",FACE,{"disambiguationData":[TD([[makeQuery(id+"F37.imprint","IMPRINT",EDGE,{"derivedFrom":subQ0}),-1.0]])]});}
            var Q1;
            {var subQ0=sQuery(id+"F37.wireOp",EDGE,"E166.1.0");Q1=makeQuery(id+"F37.imprint","IMPRINT",FACE,{"disambiguationData":[TD([[makeQuery(id+"F37.imprint","IMPRINT",EDGE,{"derivedFrom":subQ0}),1.0]])]});}
            var Q2;
            {var subQ0=sQuery(id+"F37.wireOp",EDGE,"E166.2.0");Q2=makeQuery(id+"F37.imprint","IMPRINT",FACE,{"disambiguationData":[TD([[makeQuery(id+"F37.imprint","IMPRINT",EDGE,{"derivedFrom":subQ0}),1.0]])]});}
            extrude(context, id + "F38", {"entities" : qUnion([Q0, Q1, Q2]), "depth" : 4 * mm, "offsetDistance" : 25 * mm});
        }
        {
            var Q0;
            Q0=makeQuery(id+"F5.opExtrude","SWEPT_BODY",BODY,{"disambiguationData":[OSD([sQuery(id+"F4.wireOp",EDGE,"E28"),sQuery(id+"F4.wireOp",EDGE,"E30")])]});
            var Q1;
            Q1=makeQuery(id+"F38.opExtrude","SWEPT_BODY",BODY,{"disambiguationData":[OSD([sQuery(id+"F37.wireOp",EDGE,"E156.0"),sQuery(id+"F37.wireOp",EDGE,"E157.0"),sQuery(id+"F37.wireOp",EDGE,"E160"),sQuery(id+"F37.wireOp",EDGE,"E161.MirrorCS")])]});
            var Q2;
            Q2=makeQuery(id+"F38.opExtrude","SWEPT_BODY",BODY,{"disambiguationData":[OSD([sQuery(id+"F37.wireOp",EDGE,"E156.0"),sQuery(id+"F37.wireOp",EDGE,"E157.0"),sQuery(id+"F37.wireOp",EDGE,"E163.2.0"),sQuery(id+"F37.wireOp",EDGE,"E163.2.1")])]});
            var Q3;
            Q3=makeQuery(id+"F38.opExtrude","SWEPT_BODY",BODY,{"disambiguationData":[OSD([sQuery(id+"F37.wireOp",EDGE,"E156.0"),sQuery(id+"F37.wireOp",EDGE,"E157.0"),sQuery(id+"F37.wireOp",EDGE,"E163.1.0"),sQuery(id+"F37.wireOp",EDGE,"E163.1.1")])]});
            var Q4;
            Q4=makeQuery(id+"F24.opRevolve","SWEPT_BODY",BODY,{"disambiguationData":[OSD([sQuery(id+"F1.wireOp",EDGE,"E15.MirrorCS"),sQuery(id+"F1.wireOp",EDGE,"E16.MirrorCS"),sQuery(id+"F1.wireOp",EDGE,"E14.MirrorCS"),sQuery(id+"F1.wireOp",EDGE,"E17.MirrorCS"),sQuery(id+"F1.wireOp",EDGE,"E13"),sQuery(id+"F1.wireOp",EDGE,"E18.MirrorCS")])]});
            booleanBodies(context, id + "F39", {"operationType" : BooleanOperationType.UNION, "tools" : qUnion([Q0, Q1, Q2, Q3, Q4])});
        }
        {
            var Q0;
            {var subQ0=sQuery(id+"F37.wireOp",EDGE,"E157.0");var subQ1=sQuery(id+"F37.wireOp",EDGE,"E156.0");Q0=makeQuery(id+"F39.opBoolean","MERGE",FACE,{"derivedFrom":[makeQuery(id+"F5.opExtrude","CAP_FACE",FACE,{"disambiguationData":[OSD([sQuery(id+"F4.wireOp",EDGE,"E28"),sQuery(id+"F4.wireOp",EDGE,"E30")])],"isStart":true}),makeQuery(id+"F24.opRevolve","SWEPT_FACE",FACE,{"disambiguationData":[OSD([sQuery(id+"F1.wireOp",EDGE,"E17.MirrorCS")])]}),makeQuery(id+"F38.opExtrude","CAP_FACE",FACE,{"disambiguationData":[OSD([subQ1,subQ0,sQuery(id+"F37.wireOp",EDGE,"E163.1.0"),sQuery(id+"F37.wireOp",EDGE,"E163.1.1")])],"isStart":true}),makeQuery(id+"F38.opExtrude","CAP_FACE",FACE,{"disambiguationData":[OSD([subQ1,subQ0,sQuery(id+"F37.wireOp",EDGE,"E163.2.0"),sQuery(id+"F37.wireOp",EDGE,"E163.2.1")])],"isStart":true}),makeQuery(id+"F38.opExtrude","CAP_FACE",FACE,{"disambiguationData":[OSD([subQ1,subQ0,sQuery(id+"F37.wireOp",EDGE,"E160"),sQuery(id+"F37.wireOp",EDGE,"E161.MirrorCS")])],"isStart":true})]});}
            var sketch = newSketch(context, id + "F40", { "sketchPlane" : qUnion([Q0])});
            skArc(sketch, "E167.0", {"start": v(-14.27, -14.01) * mm, "mid": v(-19.27, 5.35) * mm, "end": v(-5, 19.36) * mm});
            skArc(sketch, "E168.0", {"start": v(-5, 19.36) * mm, "mid": v(14.27, 14.01) * mm, "end": v(19.27, -5.35) * mm});
            skArc(sketch, "E169.0", {"start": v(19.27, -5.35) * mm, "mid": v(5, -19.36) * mm, "end": v(-14.27, -14.01) * mm});
            skPoint(sketch, "E170.orphan", {"position": v(-19.27, -5.35) * mm});
            skPoint(sketch, "E171.orphan", {"position": v(14.27, -14.01) * mm});
            skPoint(sketch, "E172.orphan", {"position": v(5, 19.36) * mm});
            skArc(sketch, "E173.0", {"start": v(-4.75, 18.4) * mm, "mid": v(13.56, 13.31) * mm, "end": v(18.3, -5.08) * mm});
            skArc(sketch, "E173.1", {"start": v(-13.56, -13.31) * mm, "mid": v(-18.3, 5.08) * mm, "end": v(-4.75, 18.4) * mm});
            skArc(sketch, "E173.2", {"start": v(18.3, -5.08) * mm, "mid": v(4.75, -18.4) * mm, "end": v(-13.56, -13.31) * mm});
            skArc(sketch, "E174.0", {"start": v(-7.34, 1.54) * mm, "mid": v(-6.5, 3.75) * mm, "end": v(-5, 5.6) * mm});
            skCircle(sketch, "E175", {"center": v(0, 0) * mm, "radius": 7.5 * mm});
            skCircle(sketch, "E176", {"center": v(0, 0) * mm, "radius": 8.5 * mm});
            skSolve(sketch);
        }
        {
            var Q0;
            {var subQ0=sQuery(id+"F40.wireOp",EDGE,"E168.0");var subQ1=makeQuery(id+"F38.opExtrude","CAP_EDGE",EDGE,{"disambiguationData":[OSD([sQuery(id+"F37.wireOp",EDGE,"E164")])],"isStart":true});var subQ2=makeQuery(id+"F40.imprint","INTERSECT",VERTEX,{"derivedFrom":[subQ1,subQ0]});Q0=makeQuery(id+"F40.imprint","IMPRINT",FACE,{"disambiguationData":[TD([[makeQuery(id+"F40.imprint","IMPRINT",EDGE,{"disambiguationData":[TD([[subQ2,1.0]])],"derivedFrom":subQ0}),-1.0]])]});}
            var Q1;
            {var subQ0=sQuery(id+"F40.wireOp",EDGE,"E167.0");var subQ1=makeQuery(id+"F38.opExtrude","CAP_EDGE",EDGE,{"disambiguationData":[OSD([sQuery(id+"F37.wireOp",EDGE,"E166.2.0")])],"isStart":true});var subQ2=makeQuery(id+"F40.imprint","INTERSECT",VERTEX,{"derivedFrom":[subQ1,subQ0]});Q1=makeQuery(id+"F40.imprint","IMPRINT",FACE,{"disambiguationData":[TD([[makeQuery(id+"F40.imprint","IMPRINT",EDGE,{"disambiguationData":[TD([[subQ2,-1.0]])],"derivedFrom":subQ0}),-1.0]])]});}
            var Q2;
            {var subQ0=sQuery(id+"F40.wireOp",EDGE,"E169.0");var subQ1=makeQuery(id+"F38.opExtrude","CAP_EDGE",EDGE,{"disambiguationData":[OSD([sQuery(id+"F37.wireOp",EDGE,"E166.1.0")])],"isStart":true});var subQ2=makeQuery(id+"F40.imprint","INTERSECT",VERTEX,{"derivedFrom":[subQ1,subQ0]});Q2=makeQuery(id+"F40.imprint","IMPRINT",FACE,{"disambiguationData":[TD([[makeQuery(id+"F40.imprint","IMPRINT",EDGE,{"disambiguationData":[TD([[subQ2,-1.0]])],"derivedFrom":subQ0}),-1.0]])]});}
            var Q3;
            {var subQ0=sQuery(id+"F40.wireOp",EDGE,"E175");var subQ1=makeQuery(id+"F38.opExtrude","CAP_EDGE",EDGE,{"disambiguationData":[OSD([sQuery(id+"F37.wireOp",EDGE,"E166.2.0")])],"isStart":true});var subQ2=makeQuery(id+"F40.imprint","INTERSECT",VERTEX,{"derivedFrom":[subQ1,subQ0]});var subQ3=makeQuery(id+"F38.opExtrude","CAP_EDGE",EDGE,{"disambiguationData":[OSD([sQuery(id+"F37.wireOp",EDGE,"E166.2.1")])],"isStart":true});var subQ4=makeQuery(id+"F40.imprint","INTERSECT",VERTEX,{"derivedFrom":[subQ3,subQ0]});Q3=makeQuery(id+"F40.imprint","IMPRINT",FACE,{"disambiguationData":[TD([[makeQuery(id+"F40.imprint","IMPRINT",EDGE,{"disambiguationData":[TD([[subQ2,1.0],[subQ4,-1.0]])],"derivedFrom":subQ0}),-1.0]])]});}
            var Q4;
            {var subQ0=sQuery(id+"F40.wireOp",EDGE,"E175");var subQ1=makeQuery(id+"F38.opExtrude","CAP_EDGE",EDGE,{"disambiguationData":[OSD([sQuery(id+"F37.wireOp",EDGE,"E164")])],"isStart":true});var subQ2=makeQuery(id+"F40.imprint","INTERSECT",VERTEX,{"derivedFrom":[subQ1,subQ0]});var subQ3=makeQuery(id+"F38.opExtrude","CAP_EDGE",EDGE,{"disambiguationData":[OSD([sQuery(id+"F37.wireOp",EDGE,"E165.MirrorCS")])],"isStart":true});var subQ4=makeQuery(id+"F40.imprint","INTERSECT",VERTEX,{"derivedFrom":[subQ3,subQ0]});Q4=makeQuery(id+"F40.imprint","IMPRINT",FACE,{"disambiguationData":[TD([[makeQuery(id+"F40.imprint","IMPRINT",EDGE,{"disambiguationData":[TD([[subQ2,-1.0],[subQ4,1.0]])],"derivedFrom":subQ0}),-1.0]])]});}
            var Q5;
            {var subQ0=sQuery(id+"F40.wireOp",EDGE,"E175");var subQ1=makeQuery(id+"F38.opExtrude","CAP_EDGE",EDGE,{"disambiguationData":[OSD([sQuery(id+"F37.wireOp",EDGE,"E166.1.0")])],"isStart":true});var subQ2=makeQuery(id+"F40.imprint","INTERSECT",VERTEX,{"derivedFrom":[subQ1,subQ0]});var subQ3=makeQuery(id+"F38.opExtrude","CAP_EDGE",EDGE,{"disambiguationData":[OSD([sQuery(id+"F37.wireOp",EDGE,"E166.1.1")])],"isStart":true});var subQ4=makeQuery(id+"F40.imprint","INTERSECT",VERTEX,{"derivedFrom":[subQ3,subQ0]});Q5=makeQuery(id+"F40.imprint","IMPRINT",FACE,{"disambiguationData":[TD([[makeQuery(id+"F40.imprint","IMPRINT",EDGE,{"disambiguationData":[TD([[subQ2,1.0],[subQ4,-1.0]])],"derivedFrom":subQ0}),-1.0]])]});}
            extrude(context, id + "F41", {"entities" : qUnion([Q0, Q1, Q2, Q3, Q4, Q5]), "operationType" : NewBodyOperationType.REMOVE, "oppositeDirection" : true, "depth" : 1 * mm, "offsetDistance" : 25 * mm});
        }
        {
            var Q0;
            {var subQ0=sQuery(id+"F18.wireOp",EDGE,"E135");var subQ1=sQuery(id+"F18.wireOp",EDGE,"E134");var subQ2=sQuery(id+"F18.wireOp",EDGE,"E131");var subQ3=sQuery(id+"F16.wireOp",EDGE,"E124");var subQ4=sQuery(id+"F16.wireOp",EDGE,"E123");var subQ5=sQuery(id+"F16.wireOp",EDGE,"E120");var subQ6=makeQuery(id+"F21.opBoolean","MERGE",FACE,{"derivedFrom":[makeQuery(id+"F19.opExtrude","CAP_FACE",FACE,{"disambiguationData":[OSD([subQ5,subQ4,subQ3,sQuery(id+"F18.wireOp",EDGE,"E130"),subQ2,subQ1,subQ0])],"isStart":true}),makeQuery(id+"F20.opExtrude","CAP_FACE",FACE,{"disambiguationData":[OSD([subQ5,subQ4,subQ3,sQuery(id+"F18.wireOp",EDGE,"E129"),subQ2,subQ1,subQ0])],"isStart":true})]});Q0=makeQuery(id+"F23.opBoolean","MERGE",FACE,{"derivedFrom":[makeQuery(id+"F17.opRevolve","SWEPT_FACE",FACE,{"disambiguationData":[OSD([subQ5])]}),subQ6,makeQuery(id+"F22.opPattern","COPY",FACE,{"derivedFrom":subQ6,"instanceName":"1"}),makeQuery(id+"F22.opPattern","COPY",FACE,{"derivedFrom":subQ6,"instanceName":"2"})]});}
            cPlane(context, id + "F42", {"entities" : qUnion([Q0]), "cplaneType" : CPlaneType.OFFSET, "offset" : 0 * mm, "width" : 150 * mm, "height" : 150 * mm});
        }
        {
            var Q0;
            Q0=qCreatedBy(id+"F42.planeOp",FACE);
            var sketch = newSketch(context, id + "F43", { "sketchPlane" : qUnion([Q0])});
            skCircle(sketch, "E177.0", {"center": v(-19.1, 0) * mm, "radius": 2 * mm});
            skCircle(sketch, "E178.0", {"center": v(9.55, 16.54) * mm, "radius": 2 * mm});
            skCircle(sketch, "E179.0", {"center": v(9.55, -16.54) * mm, "radius": 2 * mm});
            skArc(sketch, "E180.0.0", {"start": v(-12.64, -6.25) * mm, "mid": v(-7.05, -12.21) * mm, "end": v(0.9, -14.07) * mm, "construction": true});
            skLineSegment(sketch, "E180.0.1", {"start": v(0.9, -14.07) * mm, "end": v(4.14, -19.67) * mm, "construction": true});
            skArc(sketch, "E180.0.2", {"start": v(4.14, -19.67) * mm, "mid": v(12.68, -21.95) * mm, "end": v(14.96, -13.42) * mm, "construction": true});
            skLineSegment(sketch, "E180.0.3", {"start": v(14.96, -13.42) * mm, "end": v(11.73, -7.82) * mm, "construction": true});
            skArc(sketch, "E180.0.4", {"start": v(11.73, -7.82) * mm, "mid": v(14.1, 0) * mm, "end": v(11.73, 7.82) * mm, "construction": true});
            skLineSegment(sketch, "E180.0.5", {"start": v(11.73, 7.82) * mm, "end": v(14.96, 13.42) * mm, "construction": true});
            skArc(sketch, "E180.0.6", {"start": v(14.96, 13.42) * mm, "mid": v(12.67, 21.95) * mm, "end": v(4.14, 19.67) * mm, "construction": true});
            skLineSegment(sketch, "E180.0.7", {"start": v(4.14, 19.67) * mm, "end": v(0.9, 14.07) * mm, "construction": true});
            skArc(sketch, "E180.0.8", {"start": v(0.9, 14.07) * mm, "mid": v(-7.05, 12.21) * mm, "end": v(-12.64, 6.25) * mm, "construction": true});
            skLineSegment(sketch, "E180.0.9", {"start": v(-12.64, 6.25) * mm, "end": v(-19.1, 6.25) * mm, "construction": true});
            skArc(sketch, "E180.0.10", {"start": v(-19.1, 6.25) * mm, "mid": v(-25.35, 0) * mm, "end": v(-19.1, -6.25) * mm, "construction": true});
            skLineSegment(sketch, "E180.0.11", {"start": v(-19.1, -6.25) * mm, "end": v(-12.64, -6.25) * mm, "construction": true});
            skCircle(sketch, "E181.0", {"center": v(0, 0) * mm, "radius": 11.1 * mm, "construction": true});
            skCircle(sketch, "E182", {"center": v(0, 0) * mm, "radius": 7.5 * mm});
            skCircle(sketch, "E183", {"center": v(0, 0) * mm, "radius": 25.35 * mm});
            skCircle(sketch, "E184", {"center": v(-19.1, 0) * mm, "radius": 1.5 * mm});
            skCircle(sketch, "E185", {"center": v(9.55, 16.54) * mm, "radius": 1.5 * mm});
            skCircle(sketch, "E186", {"center": v(9.55, -16.54) * mm, "radius": 1.5 * mm});
            skSolve(sketch);
        }
        {
            var Q0;
            Q0=makeQuery(id+"F43.imprint","IMPRINT",FACE,{"disambiguationData":[TD([[makeQuery(id+"F43.imprint","IMPRINT",EDGE,{"derivedFrom":sQuery(id+"F43.wireOp",EDGE,"E177.0")}),-1.0]])]});
            var Q1;
            Q1=makeQuery(id+"F43.imprint","IMPRINT",FACE,{"disambiguationData":[TD([[makeQuery(id+"F43.imprint","IMPRINT",EDGE,{"derivedFrom":sQuery(id+"F43.wireOp",EDGE,"E177.0")}),1.0]])]});
            var Q2;
            Q2=makeQuery(id+"F43.imprint","IMPRINT",FACE,{"disambiguationData":[TD([[makeQuery(id+"F43.imprint","IMPRINT",EDGE,{"derivedFrom":sQuery(id+"F43.wireOp",EDGE,"E179.0")}),1.0]])]});
            var Q3;
            Q3=makeQuery(id+"F43.imprint","IMPRINT",FACE,{"disambiguationData":[TD([[makeQuery(id+"F43.imprint","IMPRINT",EDGE,{"derivedFrom":sQuery(id+"F43.wireOp",EDGE,"E178.0")}),1.0]])]});
            extrude(context, id + "F44", {"entities" : qUnion([Q0, Q1, Q2, Q3]), "depth" : 3 * mm, "offsetDistance" : 25 * mm});
        }
    });
